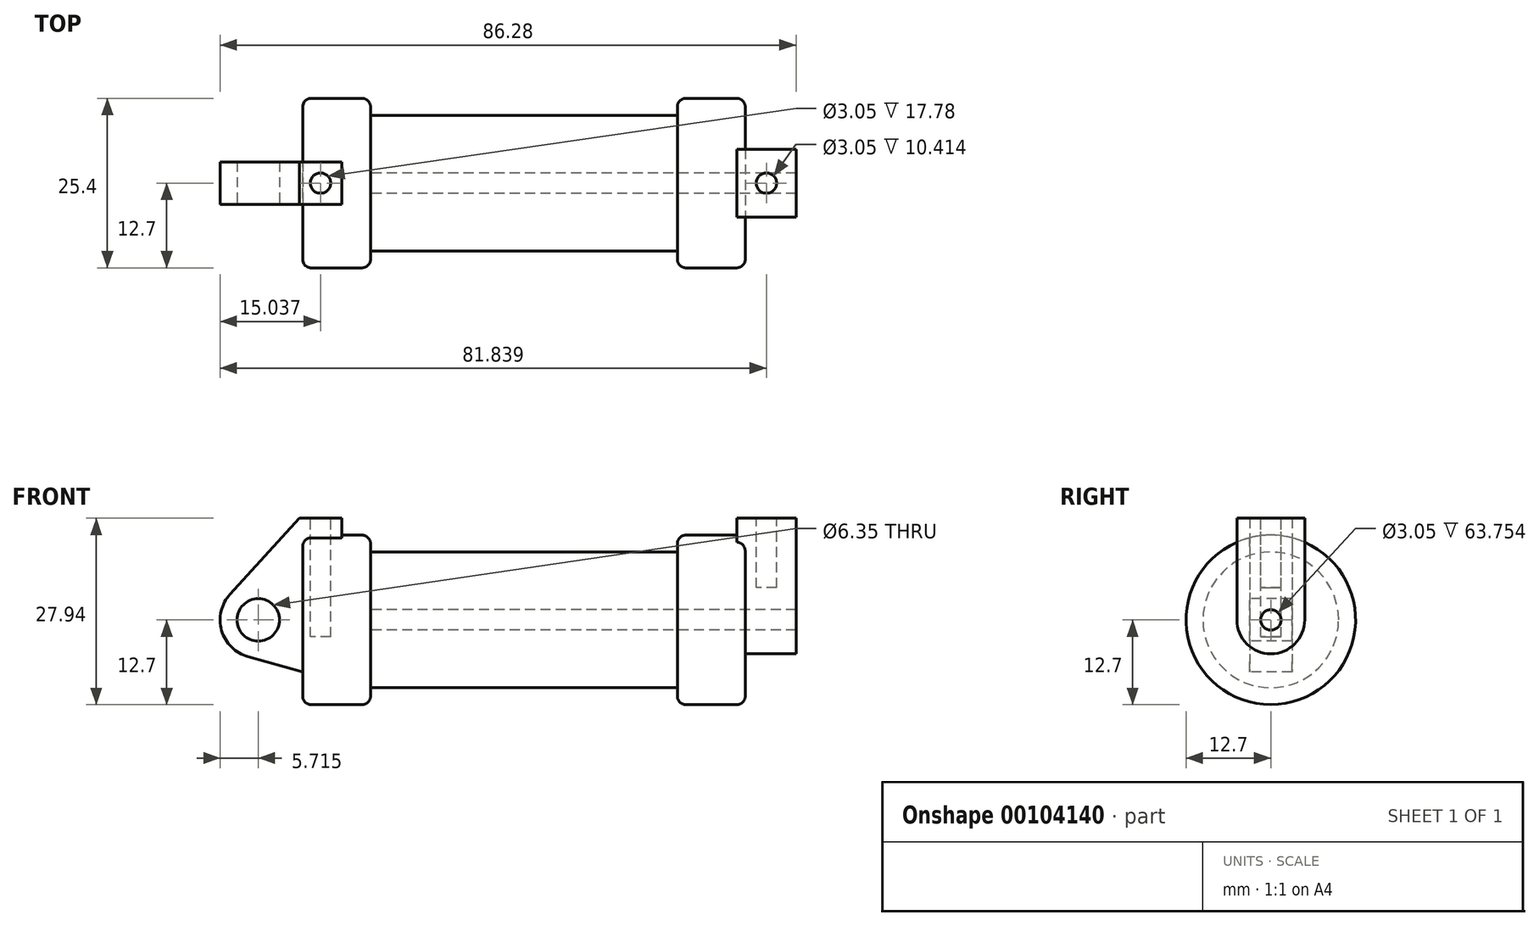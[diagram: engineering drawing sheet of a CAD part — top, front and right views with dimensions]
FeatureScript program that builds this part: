
annotation { "Feature Type Name" : "Feature", "Feature Type Description" : "" }
export const myFeature = defineFeature(function(context is Context, id is Id, definition is map)
    precondition{}
    {
        {
            var Q0;
            Q0=qCreatedBy(makeId("Front.planeOp"),FACE);
            var sketch = newSketch(context, id + "F0", { "sketchPlane" : qUnion([Q0])});
            skLineSegment(sketch, "E0", {"start": v(0, 0) * mm, "end": v(0, 12.7) * mm});
            skLineSegment(sketch, "E1", {"start": v(0, 12.7) * mm, "end": v(10.16, 12.7) * mm});
            skLineSegment(sketch, "E2", {"start": v(10.16, 12.7) * mm, "end": v(10.16, 10.16) * mm});
            skLineSegment(sketch, "E3", {"start": v(10.16, 10.16) * mm, "end": v(56.13, 10.16) * mm});
            skLineSegment(sketch, "E4", {"start": v(56.13, 10.16) * mm, "end": v(56.13, 12.7) * mm});
            skLineSegment(sketch, "E5", {"start": v(56.13, 12.7) * mm, "end": v(66.3, 12.7) * mm});
            skLineSegment(sketch, "E6", {"start": v(66.3, 12.7) * mm, "end": v(66.3, 0) * mm});
            skLineSegment(sketch, "E7", {"start": v(66.3, 0) * mm, "end": v(0, 0) * mm});
            skLineSegment(sketch, "E8", {"start": v(5.84, 15.24) * mm, "end": v(-0.5, 15.24) * mm});
            skLineSegment(sketch, "E9", {"start": v(-0.5, 15.24) * mm, "end": v(-10.88, 3.85) * mm});
            skLineSegment(sketch, "E10", {"start": v(0, 0) * mm, "end": v(-6.65, 0) * mm});
            skCircle(sketch, "E11", {"center": v(-6.65, 0) * mm, "radius": 5.72 * mm});
            skCircle(sketch, "E12", {"center": v(-6.65, 0) * mm, "radius": 3.18 * mm});
            skLineSegment(sketch, "E13", {"start": v(5.84, 15.24) * mm, "end": v(5.84, -9.4) * mm});
            skLineSegment(sketch, "E14", {"start": v(5.84, -9.4) * mm, "end": v(-8.18, -5.5) * mm});
            skSolve(sketch);
        }
        {
            var Q0;
            {var subQ0=sQuery(id+"F0.wireOp",EDGE,"E2");Q0=makeQuery(id+"F0.imprint","IMPRINT",FACE,{"disambiguationData":[TD([[makeQuery(id+"F0.imprint","IMPRINT",EDGE,{"derivedFrom":subQ0}),-1.0]])]});}
            var Q1;
            {var subQ0=sQuery(id+"F0.wireOp",EDGE,"E0");Q1=makeQuery(id+"F0.imprint","IMPRINT",FACE,{"disambiguationData":[TD([[makeQuery(id+"F0.imprint","IMPRINT",EDGE,{"derivedFrom":subQ0}),-1.0]])]});}
            var Q2;
            Q2=sQuery(id+"F0.wireOp",EDGE,"E7");
            revolve(context, id + "F1", {"entities" : qUnion([Q0, Q1]), "axis" : qUnion([Q2]), "revolveType" : RevolveType.FULL});
        }
        {
            var Q0;
            {var subQ4=sQuery(id+"F0.wireOp",EDGE,"E12");Q0=makeQuery(id+"F0.imprint","IMPRINT",FACE,{"disambiguationData":[TD([[makeQuery(id+"F0.imprint","IMPRINT",EDGE,{"derivedFrom":subQ4}),-1.0]])]});}
            var Q1;
            {var subQ3=sQuery(id+"F0.wireOp",EDGE,"E0");Q1=makeQuery(id+"F0.imprint","IMPRINT",FACE,{"disambiguationData":[TD([[makeQuery(id+"F0.imprint","IMPRINT",EDGE,{"derivedFrom":subQ3}),1.0]])]});}
            var Q2;
            {var subQ0=sQuery(id+"F0.wireOp",EDGE,"E0");Q2=makeQuery(id+"F0.imprint","IMPRINT",FACE,{"disambiguationData":[TD([[makeQuery(id+"F0.imprint","IMPRINT",EDGE,{"derivedFrom":subQ0}),-1.0]])]});}
            var Q3;
            {var subQ0=sQuery(id+"F0.wireOp",EDGE,"E14");Q3=makeQuery(id+"F0.imprint","IMPRINT",FACE,{"disambiguationData":[TD([[makeQuery(id+"F0.imprint","IMPRINT",EDGE,{"derivedFrom":subQ0}),-1.0]])]});}
            extrude(context, id + "F2", {"entities" : qUnion([Q0, Q1, Q2, Q3]), "operationType" : NewBodyOperationType.ADD, "endBound" : BoundingType.SYMMETRIC, "oppositeDirection" : true, "depth" : 6.35 * mm});
        }
        {
            var Q0;
            Q0=makeQuery(id+"F1.opRevolve","SWEPT_FACE",FACE,{"disambiguationData":[OSD([sQuery(id+"F0.wireOp",EDGE,"E6")])]});
            var sketch = newSketch(context, id + "F3", { "sketchPlane" : qUnion([Q0])});
            skCircle(sketch, "E15", {"center": v(0, 0) * mm, "radius": 5.08 * mm});
            skLineSegment(sketch, "E16", {"start": v(5.08, 0) * mm, "end": v(5.08, 15.24) * mm});
            skLineSegment(sketch, "E17", {"start": v(-5.08, 0) * mm, "end": v(-5.08, 15.24) * mm});
            skLineSegment(sketch, "E18", {"start": v(-5.08, 15.24) * mm, "end": v(5.08, 15.24) * mm});
            skCircle(sketch, "E19", {"center": v(0, 0) * mm, "radius": 1.52 * mm});
            skSolve(sketch);
        }
        {
            var Q0;
            {var subQ0=sQuery(id+"F3.wireOp",EDGE,"E18");Q0=makeQuery(id+"F3.imprint","IMPRINT",FACE,{"disambiguationData":[TD([[makeQuery(id+"F3.imprint","IMPRINT",EDGE,{"derivedFrom":subQ0}),-1.0]])]});}
            var Q1;
            Q1=makeQuery(id+"F3.imprint","IMPRINT",FACE,{"disambiguationData":[TD([[makeQuery(id+"F3.imprint","IMPRINT",EDGE,{"derivedFrom":sQuery(id+"F3.wireOp",EDGE,"E19")}),-1.0]])]});
            var Q2;
            {var subQ0=sQuery(id+"F3.wireOp",EDGE,"E16");var subQ1=sQuery(id+"F3.wireOp",EDGE,"E15");var subQ2=makeQuery(id+"F3.imprint","INTERSECT",VERTEX,{"derivedFrom":[subQ1,subQ0]});Q2=makeQuery(id+"F3.imprint","IMPRINT",FACE,{"disambiguationData":[TD([[makeQuery(id+"F3.imprint","IMPRINT",EDGE,{"disambiguationData":[TD([[subQ2,-1.0]])],"derivedFrom":subQ1}),-1.0]])]});}
            extrude(context, id + "F4", {"entities" : qUnion([Q0, Q1, Q2]), "operationType" : NewBodyOperationType.ADD, "depth" : 7.62 * mm, "hasSecondDirection" : true, "secondDirectionOppositeDirection" : true, "secondDirectionDepth" : 1.27 * mm});
        }
        {
            var Q0;
            Q0=makeQuery(id+"F4.boolean.opBoolean","SPLIT",FACE,{"disambiguationData":[TD([makeQuery(id+"F4.opExtrude","SWEPT_FACE",FACE,{"disambiguationData":[OSD([sQuery(id+"F3.wireOp",EDGE,"E19")])]})])],"derivedFrom":makeQuery(id+"F1.opRevolve","SWEPT_FACE",FACE,{"disambiguationData":[OSD([sQuery(id+"F0.wireOp",EDGE,"E6")])]})});
            var Q1;
            Q1=makeQuery(id+"F1.opRevolve","SWEPT_FACE",FACE,{"disambiguationData":[OSD([sQuery(id+"F0.wireOp",EDGE,"E2")])]});
            extrude(context, id + "F5", {"entities" : qUnion([Q0]), "operationType" : NewBodyOperationType.REMOVE, "endBound" : BoundingType.UP_TO_SURFACE, "oppositeDirection" : true, "endBoundEntityFace" : qUnion([Q1]), "depth" : 25.4 * mm});
        }
        {
            var Q0;
            Q0=makeQuery(id+"F2.opExtrude","SWEPT_FACE",FACE,{"disambiguationData":[OSD([sQuery(id+"F0.wireOp",EDGE,"E8")])]});
            var sketch = newSketch(context, id + "F6", { "sketchPlane" : qUnion([Q0])});
            skCircle(sketch, "E20", {"center": v(2.67, 0) * mm, "radius": 1.52 * mm});
            skPoint(sketch, "E20.centerSnap0", {"position": v(5.84, 0) * mm});
            skLineSegment(sketch, "E21", {"start": v(2.67, 3.18) * mm, "end": v(2.67, 1.52) * mm});
            skLineSegment(sketch, "E22.trimOffspring", {"start": v(2.67, -1.52) * mm, "end": v(2.67, -3.18) * mm});
            skSolve(sketch);
        }
        {
            var Q0;
            Q0=makeQuery(id+"F4.opExtrude","SWEPT_FACE",FACE,{"disambiguationData":[OSD([sQuery(id+"F3.wireOp",EDGE,"E18")])]});
            var sketch = newSketch(context, id + "F7", { "sketchPlane" : qUnion([Q0])});
            skLineSegment(sketch, "E23", {"start": v(69.47, 5.08) * mm, "end": v(69.47, 1.52) * mm});
            skCircle(sketch, "E24", {"center": v(69.47, 0) * mm, "radius": 1.52 * mm});
            skLineSegment(sketch, "E25.trimOffspring", {"start": v(69.47, -1.52) * mm, "end": v(69.47, -5.08) * mm});
            skSolve(sketch);
        }
        {
            var Q0;
            {var subQ0=sQuery(id+"F6.wireOp",EDGE,"E20");var subQ1=makeQuery(id+"F6.imprint","INTERSECT",VERTEX,{"derivedFrom":[subQ0,sQuery(id+"F6.wireOp",EDGE,"E21")]});Q0=makeQuery(id+"F6.imprint","IMPRINT",FACE,{"disambiguationData":[TD([[makeQuery(id+"F6.imprint","IMPRINT",EDGE,{"disambiguationData":[TD([[subQ1,-1.0]])],"derivedFrom":subQ0}),1.0]])]});}
            extrude(context, id + "F8", {"entities" : qUnion([Q0]), "operationType" : NewBodyOperationType.REMOVE, "oppositeDirection" : true, "depth" : 17.78 * mm});
        }
        {
            var Q0;
            {var subQ0=sQuery(id+"F7.wireOp",EDGE,"E24");var subQ1=makeQuery(id+"F7.imprint","INTERSECT",VERTEX,{"derivedFrom":[sQuery(id+"F7.wireOp",EDGE,"E23"),subQ0]});Q0=makeQuery(id+"F7.imprint","IMPRINT",FACE,{"disambiguationData":[TD([[makeQuery(id+"F7.imprint","IMPRINT",EDGE,{"disambiguationData":[TD([[subQ1,-1.0]])],"derivedFrom":subQ0}),1.0]])]});}
            extrude(context, id + "F9", {"entities" : qUnion([Q0]), "operationType" : NewBodyOperationType.REMOVE, "oppositeDirection" : true, "depth" : 10.4 * mm});
        }
        {
            var Q0;
            Q0=makeQuery(id+"F1.opRevolve","SWEPT_EDGE",EDGE,{"disambiguationData":[OSD([sQuery(id+"F0.wireOp",EDGE,"E4"),sQuery(id+"F0.wireOp",EDGE,"E5")])]});
            var Q1;
            Q1=makeQuery(id+"F1.opRevolve","SWEPT_EDGE",EDGE,{"disambiguationData":[OSD([sQuery(id+"F0.wireOp",EDGE,"E5"),sQuery(id+"F0.wireOp",EDGE,"E6")])]});
            var Q2;
            Q2=makeQuery(id+"F1.opRevolve","SWEPT_EDGE",EDGE,{"disambiguationData":[OSD([sQuery(id+"F0.wireOp",EDGE,"E1"),sQuery(id+"F0.wireOp",EDGE,"E2")])]});
            var Q3;
            Q3=makeQuery(id+"F1.opRevolve","SWEPT_EDGE",EDGE,{"disambiguationData":[OSD([sQuery(id+"F0.wireOp",EDGE,"E0"),sQuery(id+"F0.wireOp",EDGE,"E1")])]});
            fillet(context, id + "F10", {"entities" : qUnion([Q0, Q1, Q2, Q3]), "radius" : 1.27 * mm, "tangentPropagation" : true, "allowEdgeOverflow" : false});
        }
    });
